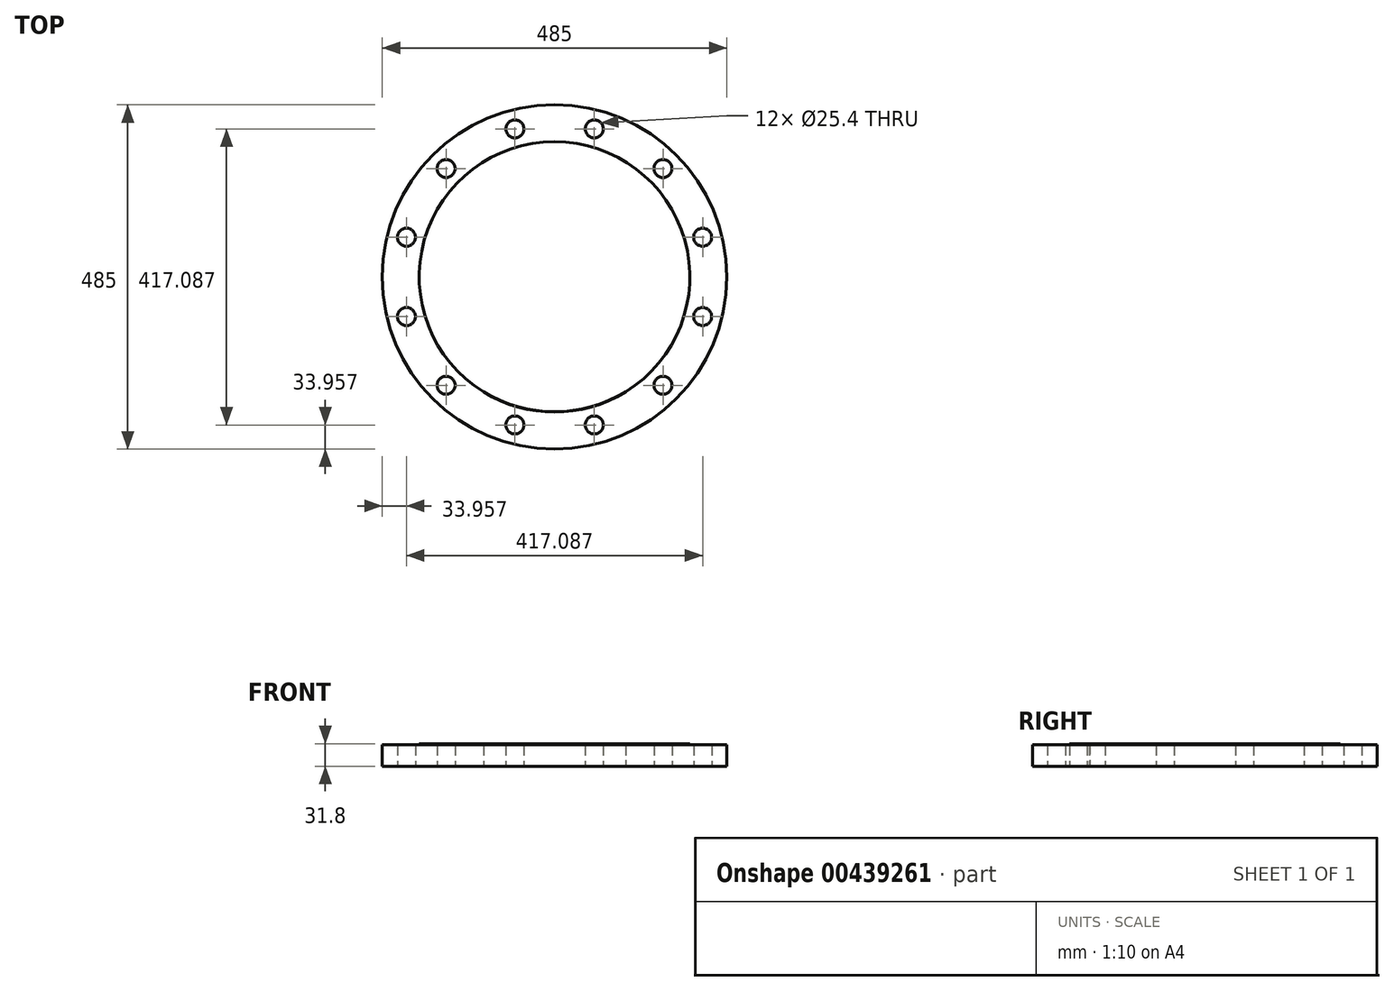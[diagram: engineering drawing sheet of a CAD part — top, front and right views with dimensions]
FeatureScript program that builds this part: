
annotation { "Feature Type Name" : "Feature", "Feature Type Description" : "" }
export const myFeature = defineFeature(function(context is Context, id is Id, definition is map)
    precondition{}
    {
        {
            assignVariable(context, id + "F0", {"name" : "THK", "anyValue" : 30.2});
        }
        {
            assignVariable(context, id + "F1", {"name" : "B", "anyValue" : 31.8});
        }
        {
            var Q0;
            Q0=qCreatedBy(makeId("Top.planeOp"),FACE);
            var sketch = newSketch(context, id + "F2", { "sketchPlane" : qUnion([Q0])});
            skCircle(sketch, "E0", {"center": v(0, 0) * mm, "radius": 215.9 * mm, "construction": true});
            skCircle(sketch, "E1", {"center": v(0, 0) * mm, "radius": 190.5 * mm});
            skCircle(sketch, "E2", {"center": v(0, 0) * mm, "radius": 242.5 * mm});
            skLineSegment(sketch, "E3", {"start": v(0, 0) * mm, "end": v(0, -311) * mm, "construction": true});
            skLineSegment(sketch, "E4", {"start": v(0, 0) * mm, "end": v(55.88, -208.54) * mm, "construction": true});
            skCircle(sketch, "E5", {"center": v(55.88, -208.54) * mm, "radius": 12.7 * mm});
            skCircle(sketch, "E6.1.0", {"center": v(152.66, -152.66) * mm, "radius": 12.7 * mm});
            skCircle(sketch, "E6.2.0", {"center": v(208.54, -55.88) * mm, "radius": 12.7 * mm});
            skCircle(sketch, "E6.3.0", {"center": v(208.54, 55.88) * mm, "radius": 12.7 * mm});
            skCircle(sketch, "E6.4.0", {"center": v(152.66, 152.66) * mm, "radius": 12.7 * mm});
            skCircle(sketch, "E6.5.0", {"center": v(55.88, 208.54) * mm, "radius": 12.7 * mm});
            skCircle(sketch, "E6.6.0", {"center": v(-55.88, 208.54) * mm, "radius": 12.7 * mm});
            skCircle(sketch, "E6.7.0", {"center": v(-152.66, 152.66) * mm, "radius": 12.7 * mm});
            skCircle(sketch, "E6.8.0", {"center": v(-208.54, 55.88) * mm, "radius": 12.7 * mm});
            skCircle(sketch, "E6.9.0", {"center": v(-208.54, -55.88) * mm, "radius": 12.7 * mm});
            skCircle(sketch, "E6.10.0", {"center": v(-152.66, -152.66) * mm, "radius": 12.7 * mm});
            skCircle(sketch, "E6.11.0", {"center": v(-55.88, -208.54) * mm, "radius": 12.7 * mm});
            skSolve(sketch);
        }
        {
            var Q0;
            Q0=makeQuery(id+"F2.imprint","IMPRINT",FACE,{"disambiguationData":[TD([[makeQuery(id+"F2.imprint","IMPRINT",EDGE,{"derivedFrom":sQuery(id+"F2.wireOp",EDGE,"E1")}),1.0]])]});
            var sketch = newSketch(context, id + "F3", { "sketchPlane" : qUnion([Q0])});
            skArc(sketch, "E7", {"start": v(-100, -161.55) * mm, "mid": v(0, -190) * mm, "end": v(100, -161.55) * mm});
            skLineSegment(sketch, "E8", {"start": v(-100, -161.55) * mm, "end": v(-100, -262) * mm});
            skLineSegment(sketch, "E9", {"start": v(100, -262) * mm, "end": v(100, -161.55) * mm});
            skLineSegment(sketch, "E10", {"start": v(-100, -262) * mm, "end": v(100, -262) * mm});
            skSolve(sketch);
        }
        {
            var Q0;
            Q0=makeQuery(id+"F2.imprint","IMPRINT",FACE,{"disambiguationData":[TD([[makeQuery(id+"F2.imprint","IMPRINT",EDGE,{"derivedFrom":sQuery(id+"F2.wireOp",EDGE,"E1")}),-1.0]])]});
            extrude(context, id + "F4", {"entities" : qUnion([Q0]), "depth" : (getVariable(context, 'THK')) * mm, "offsetDistance" : 25 * mm});
        }
        {
            var Q0;
            {var subQ0=sQuery(id+"F3.wireOp",EDGE,"E7");Q0=makeQuery(id+"F3.imprint","IMPRINT",FACE,{"disambiguationData":[TD([[makeQuery(id+"F3.imprint","IMPRINT",EDGE,{"derivedFrom":subQ0}),1.0]])]});}
            extrude(context, id + "F5", {"entities" : qUnion([Q0]), "operationType" : NewBodyOperationType.ADD, "depth" : (getVariable(context, 'B')) * mm, "offsetDistance" : 25 * mm});
        }
    });
